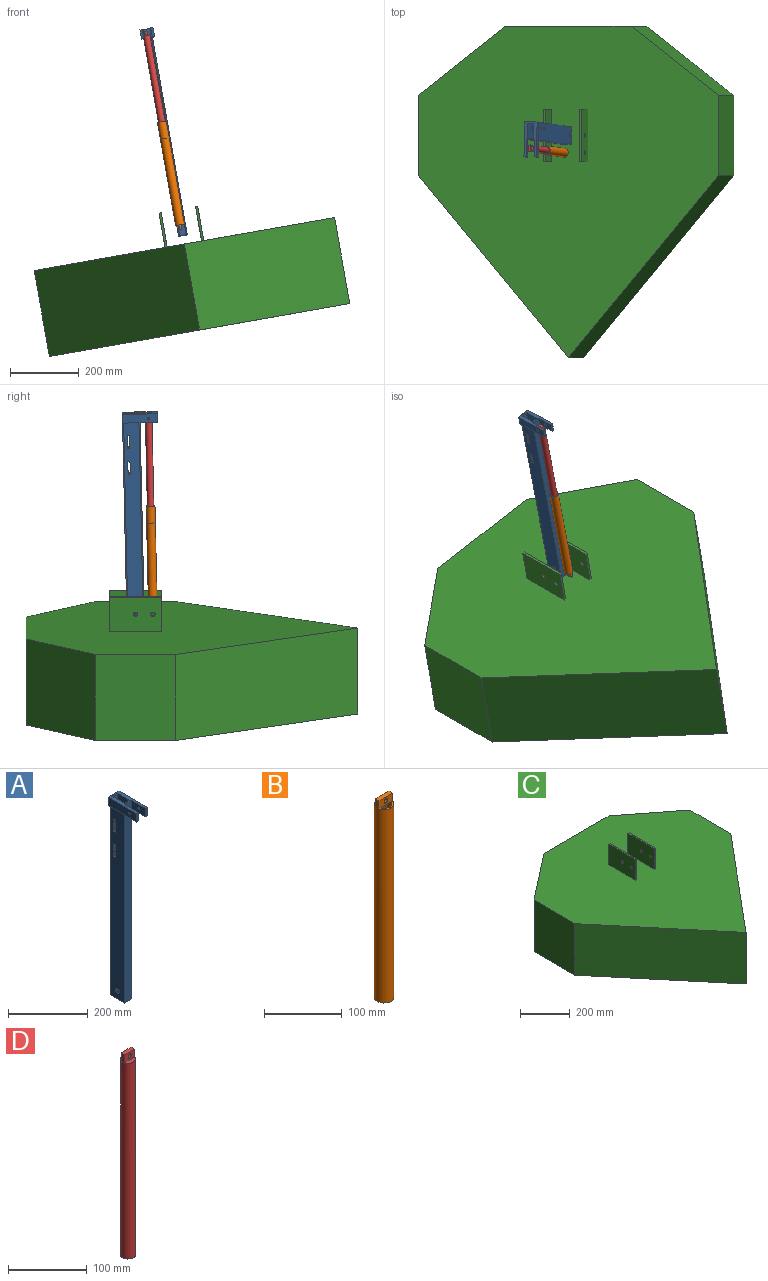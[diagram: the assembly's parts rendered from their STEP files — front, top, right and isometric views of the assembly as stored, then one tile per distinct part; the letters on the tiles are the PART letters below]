
ASSEMBLY  parts=4 mates=4
PART A: 38 faces, bbox 38.1x101.6x609.6 mm
  f0: plane 38.1x3.18mm, normal (0,1,0), area 121mm2, adj f1,f6,f23,f26
  f1: plane 6.35x3.18mm, normal (0,0,-1), area 20.2mm2, adj f0,f2,f23,f26
  f2: plane 38.1x3.18mm, normal (0,-1,0), area 121mm2, adj f1,f6,f23,f26
  f3: plane 38.1x3.18mm, normal (0,-1,0), area 121mm2, adj f4,f7,f23,f26
  f4: plane 6.35x3.18mm, normal (0,0,1), area 20.2mm2, adj f3,f5,f23,f26
  f5: plane 38.1x3.18mm, normal (0,1,0), area 121mm2, adj f4,f7,f23,f26
  f6: plane 6.35x3.18mm, normal (0,0,1), area 20.2mm2, adj f0,f2,f23,f26
  f7: plane 6.35x3.18mm, normal (0,0,-1), area 20.2mm2, adj f3,f5,f23,f26
  f8: cylinder r=7.1mm len=14.21mm, axis (-1,0,0), area 141.7mm2, adj f23,f26
  f9: plane 101.6x38.1mm, normal (0,0,1), area 1733.9mm2, adj f10,f21,f24,f25,f26,f27,f28,f29
  f10: plane 609.6x25.4mm, normal (0,-1,0), area 15483.8mm2, adj f9,f11,f22,f23,f28,f32
  f11: plane 50.8x25.4mm, normal (0,0,-1), area 443.5mm2, adj f10,f21,f22,f23,f24,f25,f26,f27
  f12: plane 38.1x3.18mm, normal (0,1,0), area 121mm2, adj f13,f18,f22,f27
  f13: plane 6.35x3.18mm, normal (0,0,-1), area 20.2mm2, adj f12,f14,f22,f27
  f14: plane 38.1x3.18mm, normal (0,-1,0), area 121mm2, adj f13,f18,f22,f27
  f15: plane 38.1x3.18mm, normal (0,-1,0), area 121mm2, adj f16,f19,f22,f27
  f16: plane 6.35x3.18mm, normal (0,0,1), area 20.2mm2, adj f15,f17,f22,f27
  f17: plane 38.1x3.18mm, normal (0,1,0), area 121mm2, adj f16,f19,f22,f27
  f18: plane 6.35x3.18mm, normal (0,0,1), area 20.2mm2, adj f12,f14,f22,f27
  f19: plane 6.35x3.18mm, normal (0,0,-1), area 20.2mm2, adj f15,f17,f22,f27
  f20: cylinder r=7.1mm len=14.21mm, axis (-1,0,0), area 141.7mm2, adj f22,f27
  f21: plane 609.6x38.1mm, normal (0,1,0), area 15806.4mm2, adj f9,f11,f22,f23,f29,f30,f33,f34
  f22: plane 584.2x50.8mm, normal (1,0,0), area 29035mm2, adj f10,f11,f12,f13,f14,f15,f16,f17
  f23: plane 584.2x50.8mm, normal (-1,0,0), area 29035mm2, adj f0,f1,f2,f3,f4,f5,f6,f7
  f24: plane 609.6x19.05mm, normal (0,-1,0), area 11612.9mm2, adj f9,f11,f26,f27
  f25: plane 609.6x19.05mm, normal (0,1,0), area 11612.9mm2, adj f9,f11,f26,f27
  f26: plane 609.6x44.45mm, normal (1,0,0), area 26454.3mm2, adj f0,f1,f2,f3,f4,f5,f6,f7
  f27: plane 609.6x44.45mm, normal (-1,0,0), area 26454.3mm2, adj f9,f11,f12,f13,f14,f15,f16,f17
  f28: plane 50.8x25.4mm, normal (1,0,0), area 1258.7mm2, adj f9,f10,f30,f31,f37
  f29: plane 101.6x25.4mm, normal (-1,0,0), area 2549mm2, adj f9,f21,f30,f31,f37
  f30: plane 101.6x6.35mm, normal (0,0,-1), area 645.2mm2, adj f21,f23,f28,f29,f31
  f31: plane 25.4x6.35mm, normal (0,-1,0), area 161.3mm2, adj f9,f28,f29,f30
  f32: plane 50.8x25.4mm, normal (-1,0,0), area 1258.7mm2, adj f9,f10,f33,f35,f36
  f33: plane 101.6x6.35mm, normal (0,0,-1), area 645.2mm2, adj f21,f22,f32,f34,f35
  f34: plane 101.6x25.4mm, normal (1,0,0), area 2549mm2, adj f9,f21,f33,f35,f36
  f35: plane 25.4x6.35mm, normal (0,-1,0), area 161.3mm2, adj f9,f32,f33,f34
  f36: cylinder r=3.17mm len=6.35mm, axis (-1,0,0), area 126.7mm2, adj f32,f34
  f37: cylinder r=3.17mm len=6.35mm, axis (-1,0,0), area 126.7mm2, adj f28,f29
PART B: 14 faces, bbox 25.4x25.4x317.5 mm
  f0: plane 24.59x9.53mm, normal (0,0,1), area 74.9mm2, adj f3,f4,f7
  f1: plane 6.35x0.4mm, normal (0,0,1), area 1.7mm2, adj f4,f10
  f2: plane 24.59x9.53mm, normal (0,0,1), area 74.9mm2, adj f3,f4,f9
  f3: cylinder r=10.16mm len=304.8mm, axis (0,0,-1), area 19457.6mm2, adj f0,f2,f6,f12
  f4: cylinder r=12.7mm len=304.8mm, axis (0,0,-1), area 24322mm2, adj f0,f1,f2,f5,f6
  f5: plane 6.35x0.4mm, normal (0,0,1), area 1.7mm2, adj f4,f8
  f6: plane 25.4x25.4mm, normal (0,0,-1), area 182.4mm2, adj f3,f4
  f7: plane 24.59x12.7mm, normal (0,1,0), area 280.7mm2, adj f0,f8,f10,f11,f12,f13
  f8: plane 12.7x6.35mm, normal (-1,0,0), area 80.6mm2, adj f5,f7,f9,f11
  f9: plane 24.59x12.7mm, normal (0,-1,0), area 280.7mm2, adj f2,f8,f10,f11,f12,f13
  f10: plane 12.7x6.35mm, normal (1,0,0), area 80.6mm2, adj f1,f7,f9,f11
  f11: plane 24.59x6.35mm, normal (0,0,1), area 156.2mm2, adj f7,f8,f9,f10
  f12: plane 20.32x6.35mm, normal (0,0,-1), area 126.9mm2, adj f3,f7,f9
  f13: cylinder r=3.17mm len=6.35mm, axis (0,-1,0), area 126.7mm2, adj f7,f9
PART C: 23 faces, bbox 887.5x965.2x355.6 mm
  f0: plane 965.2x887.47mm, normal (0,0,1), area 567109mm2, adj f1,f2,f3,f4,f5,f6,f7,f9
  f1: plane 370.01x254mm, normal (0,1,0), area 93981.4mm2, adj f0,f2,f7,f8
  f2: plane 258.73x254mm, normal (-0.61,0.79,0), area 83289.1mm2, adj f0,f1,f3,f8
  f3: plane 254x233.21mm, normal (-1,0,0), area 59236mm2, adj f0,f2,f4,f8
  f4: plane 530.53x443.73mm, normal (-0.77,-0.64,0), area 175676.3mm2, adj f0,f3,f5,f8
  f5: plane 530.53x443.73mm, normal (0.77,-0.64,0), area 175676.3mm2, adj f0,f4,f6,f8
  f6: plane 254x233.21mm, normal (1,0,0), area 59236mm2, adj f0,f5,f7,f8
  f7: plane 258.73x254mm, normal (0.61,0.79,0), area 83289.1mm2, adj f0,f1,f6,f8
  f8: plane 965.2x887.47mm, normal (0,0,-1), area 569044.5mm2, adj f1,f2,f3,f4,f5,f6,f7
  f9: plane 101.6x6.35mm, normal (0,1,0), area 645.2mm2, adj f0,f10,f12,f13
  f10: plane 152.4x101.6mm, normal (-1,0,0), area 15230.5mm2, adj f0,f9,f11,f13,f21,f22
  f11: plane 101.6x6.35mm, normal (0,-1,0), area 645.2mm2, adj f0,f10,f12,f13
  f12: plane 152.4x101.6mm, normal (1,0,0), area 15230.5mm2, adj f0,f9,f11,f13,f21,f22
  f13: plane 152.4x6.35mm, normal (0,0,1), area 967.7mm2, adj f9,f10,f11,f12
  f14: plane 101.6x6.35mm, normal (0,1,0), area 645.2mm2, adj f0,f15,f17,f18
  f15: plane 152.4x101.6mm, normal (-1,0,0), area 15230.5mm2, adj f0,f14,f16,f18,f19,f20
  f16: plane 101.6x6.35mm, normal (0,-1,0), area 645.2mm2, adj f0,f15,f17,f18
  f17: plane 152.4x101.6mm, normal (1,0,0), area 15230.5mm2, adj f0,f14,f16,f18,f19,f20
  f18: plane 152.4x6.35mm, normal (0,0,1), area 967.7mm2, adj f14,f15,f16,f17
  f19: cylinder r=6.35mm len=12.7mm, axis (-1,0,0), area 253.4mm2, adj f15,f17
  f20: cylinder r=6.35mm len=12.7mm, axis (-1,0,0), area 253.4mm2, adj f15,f17
  f21: cylinder r=6.35mm len=12.7mm, axis (-1,0,0), area 253.4mm2, adj f10,f12
  f22: cylinder r=6.35mm len=12.7mm, axis (-1,0,0), area 253.4mm2, adj f10,f12
PART D: 12 faces, bbox 19.1x19.1x317.5 mm
  f0: plane 17.96x6.35mm, normal (0,0,1), area 83.2mm2, adj f3,f6
  f1: plane 6.35x0.54mm, normal (0,0,1), area 2.3mm2, adj f3,f9
  f2: plane 17.96x6.35mm, normal (0,0,1), area 83.2mm2, adj f3,f8
  f3: cylinder r=9.53mm len=304.8mm, axis (0,0,-1), area 18241.5mm2, adj f0,f1,f2,f4,f5
  f4: plane 6.35x0.54mm, normal (0,0,1), area 2.3mm2, adj f3,f7
  f5: plane 19.05x19.05mm, normal (0,0,-1), area 285mm2, adj f3
  f6: plane 17.96x12.7mm, normal (0,1,0), area 196.4mm2, adj f0,f7,f9,f10,f11
  f7: plane 12.7x6.35mm, normal (-1,0,0), area 80.6mm2, adj f4,f6,f8,f10
  f8: plane 17.96x12.7mm, normal (0,-1,0), area 196.4mm2, adj f2,f7,f9,f10,f11
  f9: plane 12.7x6.35mm, normal (1,0,0), area 80.6mm2, adj f1,f6,f8,f10
  f10: plane 17.96x6.35mm, normal (0,0,1), area 114mm2, adj f6,f7,f8,f9
  f11: cylinder r=3.17mm len=6.35mm, axis (0,-1,0), area 126.7mm2, adj f6,f8
PLACE A rot(axis=(-0.12,-0.99,-0.01),10.1deg) t=(479.02,-369.31,-770.58)mm
PLACE B rot(axis=(0.71,0.71,0.05),172.1deg) t=(-1086.89,-871.79,-194.14)mm
PLACE C rot(axis=(0,-1,0),10deg) t=(-2318.43,-398.91,-933.43)mm fixed
PLACE D rot(axis=(-0.1,-0.08,0.99),90.3deg) t=(1780.53,-771.57,258.78)mm
MATE revolute B.f13 <-> C.f19  axis (0.98,0,0.17) through (404.15,288.22,-272.82)mm
MATE revolute A.f8 <-> C.f20  axis (0.98,0,0.17) through (416.66,339.02,-270.62)mm
MATE cylindrical D.f11 <-> A.f36  axis (0.98,0,0.17) through (304.74,300.65,290.95)mm
MATE slider D.f3 <-> B.f3  axis (0.17,-0.02,-0.98) through (329.17,297.2,134.09)mm
